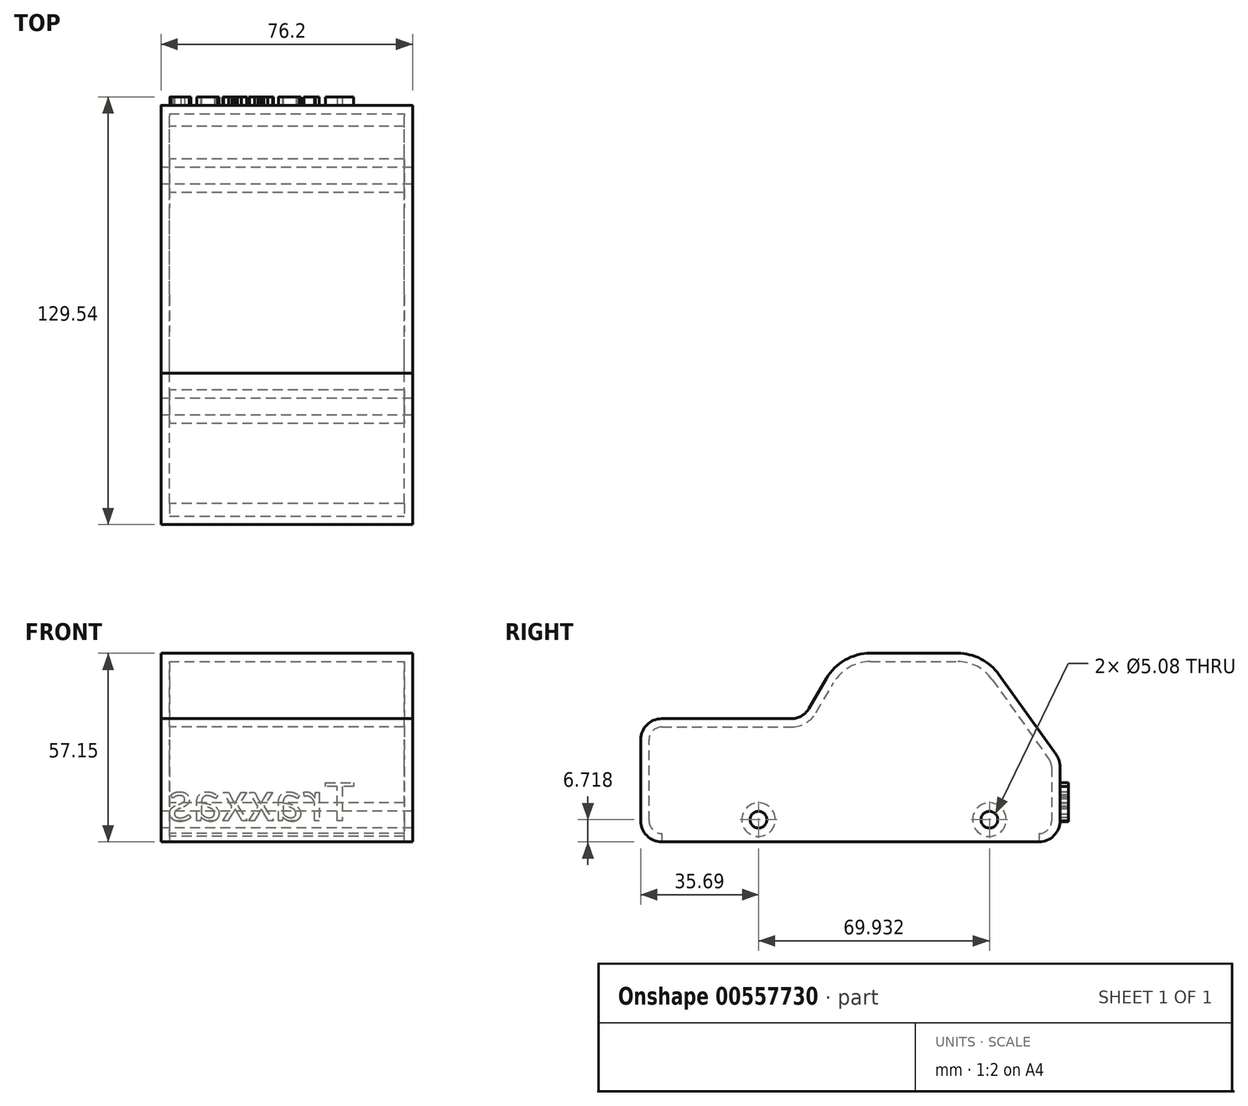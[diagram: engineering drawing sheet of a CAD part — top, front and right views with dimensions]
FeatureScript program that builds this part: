
annotation { "Feature Type Name" : "Feature", "Feature Type Description" : "" }
export const myFeature = defineFeature(function(context is Context, id is Id, definition is map)
    precondition{}
    {
        {
            var Q0;
            Q0=qCreatedBy(makeId("Right.planeOp"),FACE);
            var sketch = newSketch(context, id + "F0", { "sketchPlane" : qUnion([Q0])});
            skLineSegment(sketch, "E0", {"start": v(-21.06, 40.45) * mm, "end": v(-15.75, 49.54) * mm});
            skLineSegment(sketch, "E1", {"start": v(-2.49, 57.15) * mm, "end": v(23.97, 57.15) * mm});
            skLineSegment(sketch, "E2", {"start": v(36.48, 50.7) * mm, "end": v(53.8, 26.39) * mm});
            skLineSegment(sketch, "E3", {"start": v(54.97, 22.7) * mm, "end": v(54.97, 6.35) * mm});
            skLineSegment(sketch, "E4", {"start": v(48.62, 0) * mm, "end": v(-22.9, 0) * mm});
            skPoint(sketch, "E5.visualSharp", {"position": v(-11.3, 57.15) * mm});
            skArc(sketch, "E5.filletArc", {"start": v(-2.49, 57.15) * mm, "mid": v(-10.13, 55.11) * mm, "end": v(-15.75, 49.54) * mm});
            skPoint(sketch, "E6.visualSharp", {"position": v(31.89, 57.15) * mm});
            skArc(sketch, "E6.filletArc", {"start": v(36.48, 50.7) * mm, "mid": v(31, 55.44) * mm, "end": v(23.97, 57.15) * mm});
            skPoint(sketch, "E7.visualSharp", {"position": v(54.97, 24.74) * mm});
            skArc(sketch, "E7.filletArc", {"start": v(54.97, 22.7) * mm, "mid": v(54.67, 24.64) * mm, "end": v(53.8, 26.39) * mm});
            skLineSegment(sketch, "E8", {"start": v(-43.36, 0) * mm, "end": v(-22.9, 0) * mm});
            skPoint(sketch, "E9.visualSharp", {"position": v(-22.78, 37.52) * mm});
            skArc(sketch, "E9.filletArc", {"start": v(-26.16, 37.31) * mm, "mid": v(-23.22, 38.24) * mm, "end": v(-21.06, 40.45) * mm});
            skPoint(sketch, "E10.visualSharp", {"position": v(54.97, 0) * mm});
            skArc(sketch, "E10.filletArc", {"start": v(48.62, 0) * mm, "mid": v(53.1, 1.86) * mm, "end": v(54.97, 6.35) * mm});
            skLineSegment(sketch, "E11", {"start": v(-65.68, 0) * mm, "end": v(-43.36, 0) * mm});
            skPoint(sketch, "E12.visualSharp", {"position": v(-62.3, 0) * mm});
            skCircle(sketch, "E13", {"center": v(-36.34, 6.72) * mm, "radius": 2.54 * mm});
            skCircle(sketch, "E14", {"center": v(33.6, 6.72) * mm, "radius": 2.54 * mm});
            skLineSegment(sketch, "E15", {"start": v(-72.03, 6.35) * mm, "end": v(-72.03, 30.96) * mm});
            skLineSegment(sketch, "E16", {"start": v(-65.68, 37.31) * mm, "end": v(-26.16, 37.31) * mm});
            skPoint(sketch, "E17.visualSharp", {"position": v(-72.03, 37.31) * mm});
            skArc(sketch, "E17.filletArc", {"start": v(-65.68, 37.31) * mm, "mid": v(-70.17, 35.45) * mm, "end": v(-72.03, 30.96) * mm});
            skPoint(sketch, "E18.visualSharp", {"position": v(-72.03, 0) * mm});
            skArc(sketch, "E18.filletArc", {"start": v(-72.03, 6.35) * mm, "mid": v(-70.17, 1.86) * mm, "end": v(-65.68, 0) * mm});
            skSolve(sketch);
        }
        {
            var Q0;
            Q0 = qSketchRegion(id + "F0", true);
            extrude(context, id + "F1", {"entities" : qUnion([Q0]), "depth" : 76.2 * mm, "offsetDistance" : 25.4 * mm});
        }
        {
            var Q0;
            Q0=makeQuery(id+"F1.opExtrude","SWEPT_FACE",FACE,{"disambiguationData":[OSD([sQuery(id+"F0.wireOp",EDGE,"E4"),sQuery(id+"F0.wireOp",EDGE,"E8"),sQuery(id+"F0.wireOp",EDGE,"E11")])]});
            shell(context, id + "F2", {"entities" : qUnion([Q0]), "thickness" : 2.54 * mm});
        }
        {
            var Q0;
            Q0=makeQuery(id+"F1.opExtrude","SWEPT_FACE",FACE,{"disambiguationData":[OSD([sQuery(id+"F0.wireOp",EDGE,"E3")])]});
            var sketch = newSketch(context, id + "F3", { "sketchPlane" : qUnion([Q0])});
            skText(sketch, "E19", { "text": "Traxxas", "fontName": "NotoSansCJKsc-Regular.otf"});
            skPoint(sketch, "E20", {"position": v(-38.1, 22.7) * mm});
            const initialGuessF3  = {"E19": [-0.05887, 0.00635, 1, 0, 0.01142]};
            skSetInitialGuess(sketch, initialGuessF3);
            skSolve(sketch);
        }
        {
            var Q0;
            Q0 = qSketchRegion(id + "F3", true);
            extrude(context, id + "F4", {"entities" : qUnion([Q0]), "operationType" : NewBodyOperationType.ADD, "depth" : 2.54 * mm, "offsetDistance" : 25.4 * mm});
        }
    });
